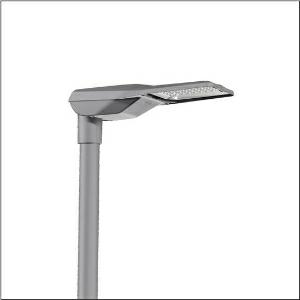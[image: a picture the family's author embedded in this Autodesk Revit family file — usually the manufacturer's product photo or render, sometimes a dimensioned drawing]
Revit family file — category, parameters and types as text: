
# Revit family: streetlight_sl_21_iq_mini___stw1_0a_5xe2e41g08gb_cbe1
name_source: partatom
category: Lighting Fixtures
units: mm (PartAtom-declared; Revit-internal decimal feet)

## family parameters
Cut with Voids When Loaded = No
Host = Face
Light Source = No
Part Type = Normal
Room Calculation Point = No
Round Connector Dimension = Use Diameter
Shared = No

## types (1)
- --- (1 x LED, 5920 lm, 37.1 W, 4000K)
    Apparent Load = 37 VA
    CIE Flux Codes = 38 75 98 100 100
    Color Rendering = 70
    Color Temperature = 4000K
    Default Elevation = 1800 mm
    Description = Streetlight SL 21 iQ mini, mast luminaire, primary light control with lens, of PMMA, primary optical cover: cover, of toughened safety glass, transparent, light distribution: STW1.0a, light emission: direct distribution, primary light characteristic: asymmetric, installation type: post-top, side-entry, LED, High Power LED, rated luminous flux: 5.920lm, luminous efficacy: 160lm/W, light colour: 740, colour temperature: 4000K, control gear: iQ Street-Remote, control: Street-Remote, Auto-Match, Temp-Guard, Lumen-Switch, Night-Set, Smart-Wire, Light-Fading, Desk-Remote (wireless, voltage-free reading and setting of iQ features in the workshop via application-optimized NFC function/RFID function), optimised constant luminous flux control (CLO 2.0), pre-setting: linear dimming characteristic, mains connection: 220..240V, AC, 50/60Hz, start of lifetime: 37W, end of service life: 39W, reduction: 18W, luminaire housing, of diecast aluminium, powder-coated, SITECO metallic grey (DB 702S), corrosivity category C5 high according to DIN EN ISO 12944, please order mast flange separately, inclination adjustable: 0°, 5°, 10°, 15°, sealing non-destructively replaceable, multi-level sealing system, length: 628mm, width: 235mm, height: 110mm, mast flange for spigot size: 42mm (side-entry): 5XC10008XM4, 60/48mm (side-entry/post-top): 5XC10108XM2, 76/60mm (side-entry/post-top): 5XC10108XM1, mounting height: 4..8m, protection rating (complete): IP66, insulation class (complete): insulation class II (safety insulation), certification: CE, ENEC, ENEC+, VDE, impact resistance: IK10, permissible operating ambient temperature for outdoor applications: -40..+50°C, standard-compliant lighting for roads and squares, packaging unit: 1 piece

Light Distribution: STW1.0a
    Height = 110 mm
    Lamp = 1 x LED
    Lamp Light Flux = 5920 lm
    Lamp Power = 37.1 W
    Lamp count = 1
    Length = 625 mm
    Luminous efficacy = 160 lm/W
    Manufacturer = Siteco
    ModVariant = No
    Model = 5XE2E41G08GB
    Number of Poles = 1
    OnlyDefault = Yes
    Power Factor = 1
    Product Name = Streetlight SL 21 iQ mini | STW1.0a
    Product group = mast luminaire | pylon top
    ProductGroupID = 6100
    Protection Class = Protection class II
    Protection Degree = IP 66
    RLX_Detail_Level = 1
    RLX_Emergency_Light_Flux = 0 lm
    RLX_Emergency_Type = 0
    RLX_Emergency_Type_DB = No
    RlxData = <blob elided: 26417 chars, md5=8ff799ff>
    Socket = socket
    Standby Power = 0 W
    System Light Flux = 5920 lm
    System Power = 37 W
    Type Comments = factory setting: luminous flux: 100 % | dim-lin: 254 | 385 mA
    Type Image = l_1003519.jpg
    URL = http://relux.com
    VarID = @adj_184947
    Voltage = 0 V
    Weight = 0.00 kg
    Width = 234 mm

## geometry (parser evidence)
native form markers: Blend x4, Sweep x11
no freeform markers — native parametric forms only
